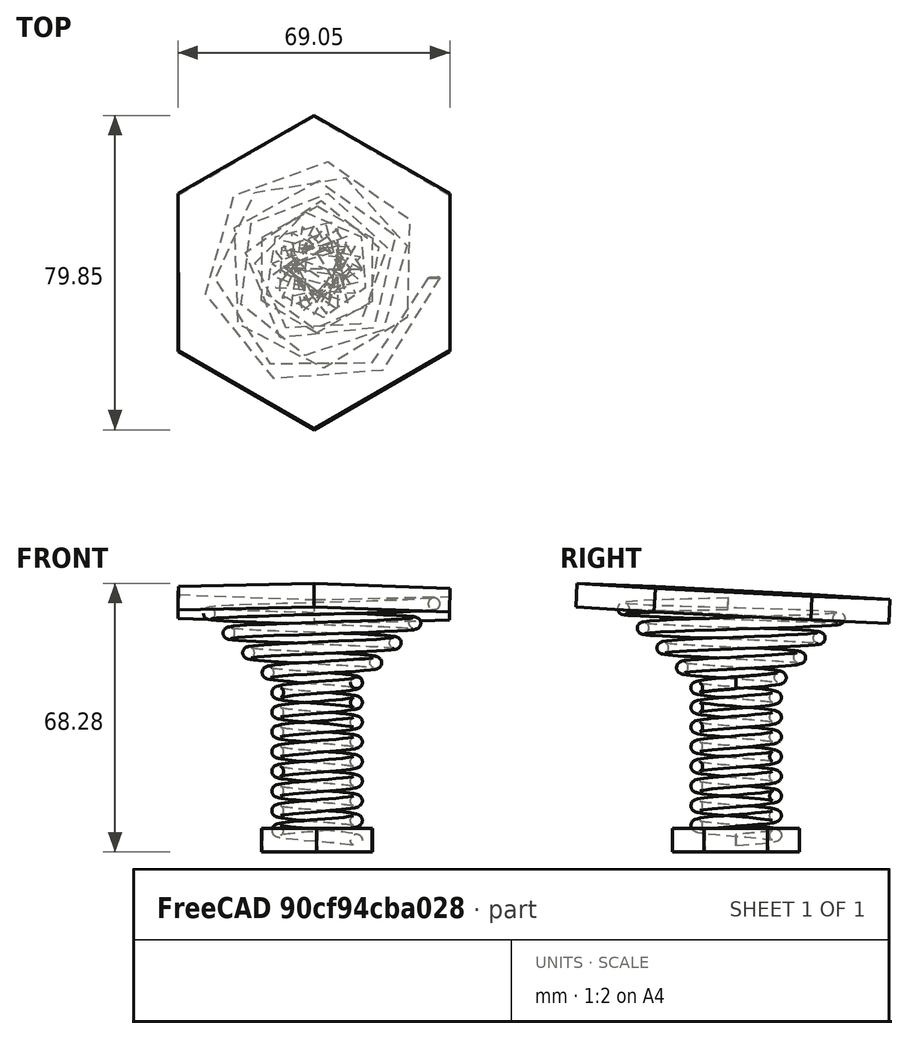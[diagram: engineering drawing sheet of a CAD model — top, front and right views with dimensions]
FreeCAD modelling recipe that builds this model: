
FCSTD DOCUMENT  (FreeCAD 0.21R33668 +26 (Git))
Label: Ressort-essai2-1-FEM
License: All rights reserved
LicenseURL: http://en.wikipedia.org/wiki/All_rights_reserved
objects: Sketcher::SketchObject×3, Part::Helix×2, Part::Sweep×2, PartDesign::Plane×2, PartDesign::Pad×2, PartDesign::Body×2, PartDesign::ShapeBinder×1, Fem::FemMeshShapeNetgenObject×1, Fem::FemSolverObjectPython×1, App::MaterialObjectPython×1, Fem::ConstraintFixed×1, Fem::ConstraintForce×1, Fem::FemAnalysis×1
note: 16 computed .brp shape members not serialized (recipe doc carries the construction recipe); baked Part::Feature solids carry a one-line shape summary decoded from their .brp

FEATURE [Part::Helix] Helix  label="Hélice"
  Angle = 0
  AttacherType = Attacher::AttachEngine3D
  Height = 40
  LocalCoord = 0
  Pitch = 5
  Radius = 10
  SegmentLength = 0
  Style = 1
FEATURE [Sketcher::SketchObject] Sketch  label="Profile"
  FullyConstrained = true
  MapMode = 5
  Placement = pos=(0,0,0) rot=(1,0,0;1.5708rad)
  Support = -> [XZ_Plane]
  sketch-geometry (1):
    g0: Circle CenterX=10 CenterY=0 CenterZ=0 NormalX=0 NormalY=0 NormalZ=1 AngleXU=0 Radius=1.5
  constraints (3):
    c: PointOnObject(g0,g-1)
    c: Radius(g0) = 1.5
    c: DistanceX(g-1,g0) = 10
FEATURE [Part::Sweep] Sweep
  Frenet = true
  Sections = -> [Sketch]
  Solid = true
  Spine = -> Helix
  Transition = 1
FEATURE [Part::Helix] Helix001  label="Hélice001"
  Angle = 45
  AttacherType = Attacher::AttachEngine3D
  Height = 20
  LocalCoord = 0
  Pitch = 5
  Placement = pos=(0,0,40) rot=(0,0,1;0rad)
  Radius = 10
  SegmentLength = 0
  Style = 1
FEATURE [Part::Sweep] Sweep001
  Frenet = true
  Placement = pos=(0,0,40) rot=(0,0,1;0rad)
  Sections = -> [Sketch]
  Solid = true
  Spine = -> Helix001
  Transition = 1
FEATURE [PartDesign::Plane] DatumPlane
  Length = 60
  MapMode = 3
  Placement = pos=(0,0,0) rot=(1,0,0;3.14159rad)
  ResizeMode = 0
  Support = -> [Sketch]
  Width = 60
FEATURE [Sketcher::SketchObject] Sketch001
  FullyConstrained = false
  MapMode = 5
  Placement = pos=(0,0,0) rot=(1,0,0;3.14159rad)
  Support = -> [DatumPlane]
  sketch-geometry (7):
    g0: LineSegment StartX=13.9076 StartY=8.18793 StartZ=0 EndX=-0.137134 EndY=16.1383 EndZ=0
    g1: LineSegment StartX=-0.137134 StartY=16.1383 StartZ=0 EndX=-14.0448 EndY=7.95041 EndZ=0
    g2: LineSegment StartX=-14.0448 StartY=7.95041 StartZ=0 EndX=-13.9076 EndY=-8.18793 EndZ=0
    g3: LineSegment StartX=-13.9076 StartY=-8.18793 StartZ=0 EndX=0.137134 EndY=-16.1383 EndZ=0
    g4: LineSegment StartX=0.137134 StartY=-16.1383 StartZ=0 EndX=14.0448 EndY=-7.95041 EndZ=0
    g5: LineSegment StartX=14.0448 StartY=-7.95041 StartZ=0 EndX=13.9076 EndY=8.18793 EndZ=0
    g6: Circle CenterX=0 CenterY=0 CenterZ=0 NormalX=0 NormalY=0 NormalZ=1 AngleXU=0 Radius=16.1389
  constraints (14):
    c: Coincident(g0,g1)
    c: Coincident(g1,g2)
    c: Coincident(g2,g3)
    c: Coincident(g3,g4)
    c: Coincident(g4,g5)
    c: Coincident(g5,g0)
    c: Equal(g0, g1-g5) x5
    c: PointOnObject(g0,g6)
    c: PointOnObject(g1,g6)
    c: PointOnObject(g2,g6)
    c: PointOnObject(g3,g6)
    c: PointOnObject(g4,g6)
    c: PointOnObject(g5,g6)
    c: Coincident(g6,g-1)
FEATURE [PartDesign::Pad] Pad
  Direction = (0,-2e-16,-1)
  Length = 6
  Length2 = 10
  Midplane = true
  Placement = pos=(0,0,0) rot=(1,0,0;3.14159rad)
  Profile = -> Sketch001
  ReferenceAxis = -> Sketch001 [N_Axis]
  Type = 0
FEATURE [PartDesign::Body] Body
  Group = -> [Sketch,DatumPlane,Sketch001,Pad]
  Origin = -> Origin
  Tip = -> Pad
FEATURE [PartDesign::ShapeBinder] ReferenceSweep001
  Placement = pos=(0,0,40) rot=(0,0,1;0rad)
  Support = -> [Sweep001]
  TraceSupport = false
FEATURE [PartDesign::Plane] DatumPlane001
  Length = 97.5241
  MapMode = 8
  Placement = pos=(31.2223,-2.01915,60.0415) rot=(0.999638,0.026587,-0.004143;3.08931rad)
  ResizeMode = 0
  Support = -> [ReferenceSweep001]
  Width = 109.064
FEATURE [Sketcher::SketchObject] Sketch002
  FullyConstrained = false
  MapMode = 5
  Placement = pos=(31.2223,-2.01915,60.0415) rot=(0.999638,0.026587,-0.004143;3.08931rad)
  Support = -> [DatumPlane001]
  sketch-geometry (7):
    g0: LineSegment StartX=3.5913 StartY=-20.9796 StartZ=0 EndX=1.49521 EndY=18.7911 EndZ=0
    g1: LineSegment StartX=1.49521 StartY=18.7911 StartZ=0 EndX=-33.9952 EndY=36.8611 EndZ=0
    g2: LineSegment StartX=-33.9952 StartY=36.8611 StartZ=0 EndX=-67.3896 EndY=15.1605 EndZ=0
    g3: LineSegment StartX=-67.3896 StartY=15.1605 StartZ=0 EndX=-65.2935 EndY=-24.6101 EndZ=0
    g4: LineSegment StartX=-65.2935 StartY=-24.6101 StartZ=0 EndX=-29.803 EndY=-42.6802 EndZ=0
    g5: LineSegment StartX=-29.803 StartY=-42.6802 StartZ=0 EndX=3.5913 EndY=-20.9796 EndZ=0
    g6: Circle CenterX=-31.8991 CenterY=-2.90951 CenterZ=0 NormalX=0 NormalY=0 NormalZ=1 AngleXU=0 Radius=39.8259
  constraints (13):
    c: Coincident(g0,g1)
    c: Coincident(g1,g2)
    c: Coincident(g2,g3)
    c: Coincident(g3,g4)
    c: Coincident(g4,g5)
    c: Coincident(g5,g0)
    c: Equal(g0, g1-g5) x5
    c: PointOnObject(g0,g6)
    c: PointOnObject(g1,g6)
    c: PointOnObject(g2,g6)
    c: PointOnObject(g3,g6)
    c: PointOnObject(g4,g6)
    c: PointOnObject(g5,g6)
FEATURE [PartDesign::Pad] Pad001
  Direction = (-0.00688828,-0.0524625,-0.998599)
  Length = 6
  Length2 = 10
  Midplane = true
  Placement = pos=(31.2223,-2.01915,60.0415) rot=(0.999638,0.026587,-0.004143;3.08931rad)
  Profile = -> Sketch002
  ReferenceAxis = -> Sketch002 [N_Axis]
  Type = 0
FEATURE [PartDesign::Body] Body001  label="Corps"
  Group = -> [DatumPlane001,ReferenceSweep001,Sketch002,Pad001]
  Origin = -> Origin001
  Tip = -> Pad001
FEATURE [Fem::FemMeshShapeNetgenObject] FEMMeshNetgen
  Fineness = 2
  GrowthRate = 0.3
  MaxSize = 1000
  NbSegsPerEdge = 1
  NbSegsPerRadius = 2
  Optimize = true
  SecondOrder = true
  Shape = -> Sweep
FEATURE [Fem::FemSolverObjectPython] SolverCcxTools  # FEM object (typed FeaturePython)
  AnalysisType = 0
  BeamShellResultOutput3D = false
  BucklingFactors = 1
  EigenmodeHighLimit = 1000000
  EigenmodeLowLimit = 0
  EigenmodesCount = 10
  GeometricalNonlinearity = 0
  IterationsControlParameterCutb = 0.25,0.5,0.75,0.85,,,1.5,
  IterationsControlParameterIter = 4,8,9,200,10,400,,200,,
  IterationsControlParameterTimeUse = false
  IterationsThermoMechMaximum = 200
  IterationsUserDefinedIncrementations = false
  IterationsUserDefinedTimeStepLength = false
  MaterialNonlinearity = 0
  MatrixSolverType = 0
  SplitInputWriter = false
  ThermoMechSteadyState = true
  TimeEnd = 1
  TimeInitialStep = 1
FEATURE [App::MaterialObjectPython] MaterialSolid  # material (typed FeaturePython)
  Category = 0
  Material = AuthorAndLicense=(c) 2013 Juergen Riegel (CC-BY 3.0); CardName=CalculiX-Steel; Density=7900 kg/m^3; Description=Standard steel material for CalculiX sample calculations; Father=Metal; Name=CalculiX-Steel; PoissonRatio=0.3; SpecificHeat=590 J/kg/K; ThermalConductivity=43 W/m/K; ThermalExpansionCoefficient=0.000012 m/m/K; YoungsModulus=210000 MPa
FEATURE [Fem::ConstraintFixed] ConstraintFixed
  NormalDirection = (0.00688828,0.0524625,0.998599)
  Normals = (4) [(0.00688828,0.0524625,0.998599),(0.00688828,0.0524625,0.998599),(0.00688828,0.0524625,0.998599),(0.00688828,0.0524625,0.998599)]
  Points = (4) [(10.7359,-13.909,63.8117),(10.7359,12.605,62.4188),(-12.2663,-13.9007,63.9699),(-12.2663,12.6133,62.577)]
  References = -> [Pad001]
  Scale = 8
FEATURE [Fem::ConstraintForce] ConstraintForce
  DirectionVector = (0,-2e-16,-1)
  Force = 1
  NormalDirection = (0,-2e-16,-1)
  Points = (4) [(4.68159,-5.37945,-3),(4.68159,5.37945,-3),(-4.68159,-5.37945,-3),(-4.68159,5.37945,-3)]
  References = -> [Pad]
  Scale = 4
FEATURE [Fem::FemAnalysis] Analysis
  Group = -> [FEMMeshNetgen,SolverCcxTools,MaterialSolid,ConstraintFixed,ConstraintForce]
